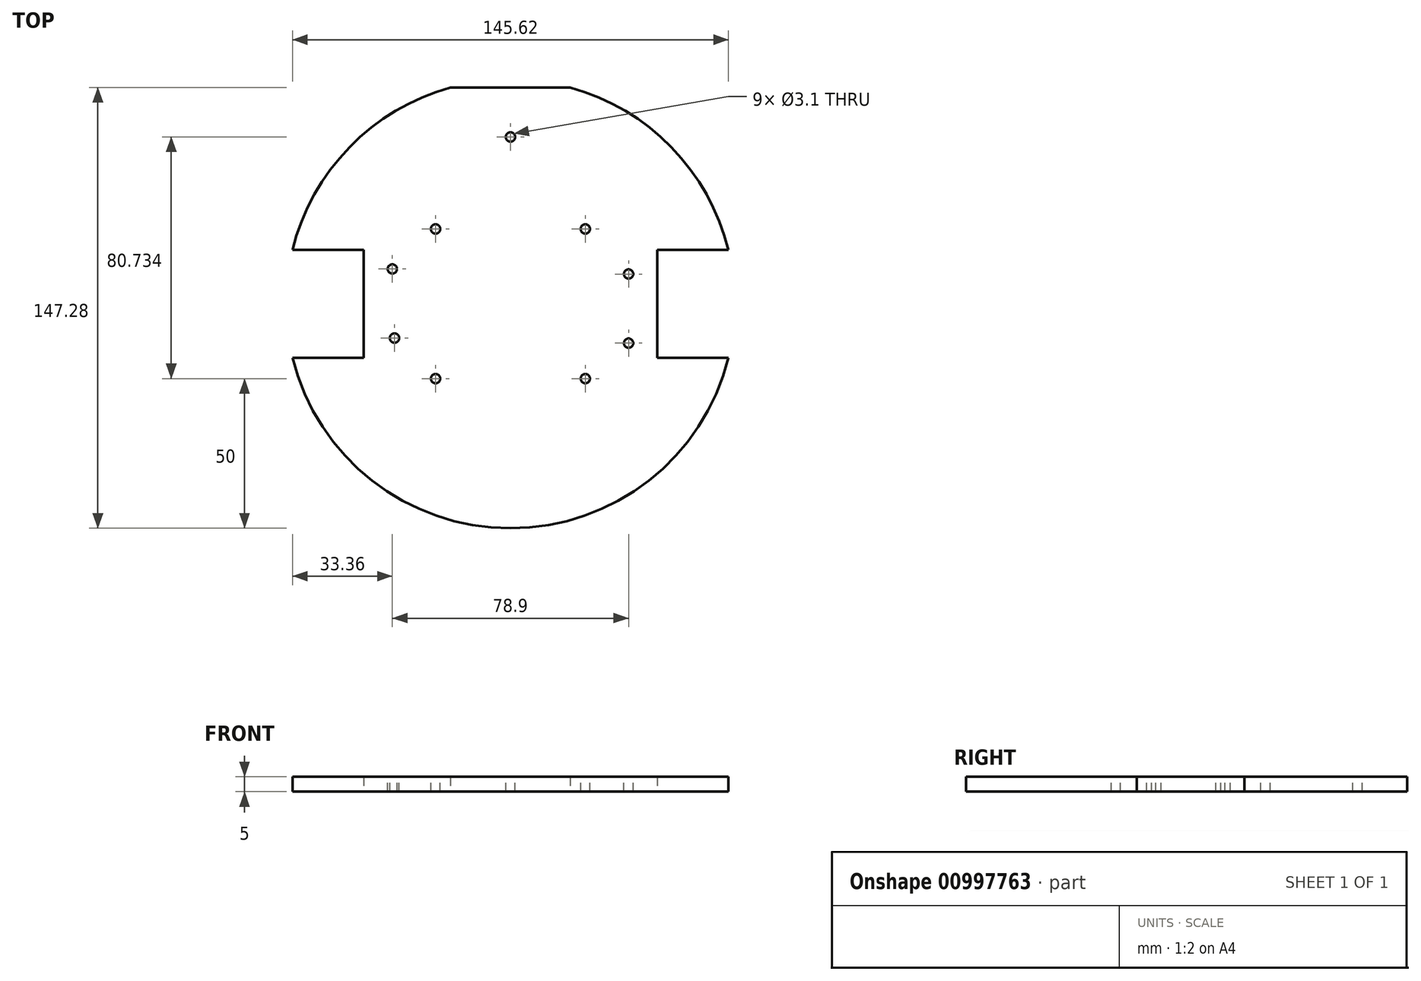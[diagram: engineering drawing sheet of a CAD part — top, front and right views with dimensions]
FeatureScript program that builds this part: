
annotation { "Feature Type Name" : "Feature", "Feature Type Description" : "" }
export const myFeature = defineFeature(function(context is Context, id is Id, definition is map)
    precondition{}
    {
        {
            var Q0;
            Q0=qCreatedBy(makeId("Top.planeOp"),FACE);
            var sketch = newSketch(context, id + "F0", { "sketchPlane" : qUnion([Q0])});
            skCircle(sketch, "E0", {"center": v(0, 0) * mm, "radius": 75 * mm});
            skSolve(sketch);
        }
        {
            var Q0;
            Q0=makeQuery(id+"F0.imprint","IMPRINT",FACE,{"disambiguationData":[TD([[makeQuery(id+"F0.imprint","IMPRINT",EDGE,{"derivedFrom":sQuery(id+"F0.wireOp",EDGE,"E0")}),1.0]])]});
            extrude(context, id + "F1", {"entities" : qUnion([Q0]), "depth" : 5 * mm, "offsetDistance" : 25 * mm});
        }
        {
            var Q0;
            Q0=qCreatedBy(makeId("Top.planeOp"),FACE);
            var sketch = newSketch(context, id + "F2", { "sketchPlane" : qUnion([Q0])});
            skLineSegment(sketch, "E1.bottom", {"start": v(75, -18) * mm, "end": v(49, -18) * mm});
            skLineSegment(sketch, "E1.top", {"start": v(75, 18) * mm, "end": v(49, 18) * mm});
            skLineSegment(sketch, "E1.left", {"start": v(75, -18) * mm, "end": v(75, 18) * mm});
            skLineSegment(sketch, "E1.right", {"start": v(49, -18) * mm, "end": v(49, 18) * mm});
            skSolve(sketch);
        }
        {
            var Q0;
            Q0=makeQuery(id+"F2.imprint","IMPRINT",FACE,{"disambiguationData":[TD([[makeQuery(id+"F2.imprint","IMPRINT",EDGE,{"derivedFrom":sQuery(id+"F2.wireOp",EDGE,"E1.bottom")}),-1.0]])]});
            extrude(context, id + "F3", {"entities" : qUnion([Q0]), "operationType" : NewBodyOperationType.REMOVE, "depth" : 25 * mm, "offsetDistance" : 25 * mm});
        }
        {
            var Q0;
            Q0=qCreatedBy(makeId("Top.planeOp"),FACE);
            var sketch = newSketch(context, id + "F4", { "sketchPlane" : qUnion([Q0])});
            skLineSegment(sketch, "E2.bottom", {"start": v(-49, -18) * mm, "end": v(-75, -18) * mm});
            skLineSegment(sketch, "E2.top", {"start": v(-49, 18) * mm, "end": v(-75, 18) * mm});
            skLineSegment(sketch, "E2.left", {"start": v(-49, -18) * mm, "end": v(-49, 18) * mm});
            skLineSegment(sketch, "E2.right", {"start": v(-75, -18) * mm, "end": v(-75, 18) * mm});
            skSolve(sketch);
        }
        {
            var Q0;
            Q0=makeQuery(id+"F4.imprint","IMPRINT",FACE,{"disambiguationData":[TD([[makeQuery(id+"F4.imprint","IMPRINT",EDGE,{"derivedFrom":sQuery(id+"F4.wireOp",EDGE,"E2.bottom")}),-1.0]])]});
            extrude(context, id + "F5", {"entities" : qUnion([Q0]), "operationType" : NewBodyOperationType.REMOVE, "depth" : 25 * mm, "offsetDistance" : 25 * mm});
        }
        {
            var Q0;
            Q0=qCreatedBy(makeId("Top.planeOp"),FACE);
            var sketch = newSketch(context, id + "F6", { "sketchPlane" : qUnion([Q0])});
            skLineSegment(sketch, "E3.bottom", {"start": v(20, 78) * mm, "end": v(-20, 78) * mm});
            skLineSegment(sketch, "E3.top", {"start": v(20, 72.28) * mm, "end": v(-20, 72.28) * mm});
            skLineSegment(sketch, "E3.left", {"start": v(20, 78) * mm, "end": v(20, 72.28) * mm});
            skLineSegment(sketch, "E3.right", {"start": v(-20, 78) * mm, "end": v(-20, 72.28) * mm});
            skSolve(sketch);
        }
        {
            var Q0;
            Q0=makeQuery(id+"F6.imprint","IMPRINT",FACE,{"disambiguationData":[TD([[makeQuery(id+"F6.imprint","IMPRINT",EDGE,{"derivedFrom":sQuery(id+"F6.wireOp",EDGE,"E3.bottom")}),1.0]])]});
            extrude(context, id + "F7", {"entities" : qUnion([Q0]), "operationType" : NewBodyOperationType.REMOVE, "depth" : 25 * mm, "offsetDistance" : 25 * mm});
        }
        {
            var Q0;
            Q0=makeQuery(id+"F1.opExtrude","CAP_FACE",FACE,{"disambiguationData":[OSD([sQuery(id+"F0.wireOp",EDGE,"E0")])],"isStart":false});
            var sketch = newSketch(context, id + "F8", { "sketchPlane" : qUnion([Q0])});
            skCircle(sketch, "E4", {"center": v(-25, 25) * mm, "radius": 1.55 * mm});
            skCircle(sketch, "E5", {"center": v(25, 25) * mm, "radius": 1.55 * mm});
            skCircle(sketch, "E6", {"center": v(-25, -25) * mm, "radius": 1.55 * mm});
            skCircle(sketch, "E7", {"center": v(25, -25) * mm, "radius": 1.55 * mm});
            skSolve(sketch);
        }
        {
            var Q0;
            Q0=makeQuery(id+"F8.imprint","IMPRINT",FACE,{"disambiguationData":[TD([[makeQuery(id+"F8.imprint","IMPRINT",EDGE,{"derivedFrom":sQuery(id+"F8.wireOp",EDGE,"E6")}),1.0]])]});
            var Q1;
            Q1=makeQuery(id+"F8.imprint","IMPRINT",FACE,{"disambiguationData":[TD([[makeQuery(id+"F8.imprint","IMPRINT",EDGE,{"derivedFrom":sQuery(id+"F8.wireOp",EDGE,"E4")}),1.0]])]});
            var Q2;
            Q2=makeQuery(id+"F8.imprint","IMPRINT",FACE,{"disambiguationData":[TD([[makeQuery(id+"F8.imprint","IMPRINT",EDGE,{"derivedFrom":sQuery(id+"F8.wireOp",EDGE,"E5")}),1.0]])]});
            var Q3;
            Q3=makeQuery(id+"F8.imprint","IMPRINT",FACE,{"disambiguationData":[TD([[makeQuery(id+"F8.imprint","IMPRINT",EDGE,{"derivedFrom":sQuery(id+"F8.wireOp",EDGE,"E7")}),1.0]])]});
            var Q4;
            Q4=sQuery(id+"F8.wireOp",EDGE,"E6");
            var Q5;
            Q5=sQuery(id+"F8.wireOp",EDGE,"E4");
            var Q6;
            Q6=sQuery(id+"F8.wireOp",EDGE,"E5");
            var Q7;
            Q7=sQuery(id+"F8.wireOp",EDGE,"E7");
            extrude(context, id + "F9", {"entities" : qUnion([Q0, Q1, Q2, Q3]), "operationType" : NewBodyOperationType.REMOVE, "surfaceEntities" : qUnion([Q4, Q5, Q6, Q7]), "oppositeDirection" : true, "depth" : 25 * mm, "offsetDistance" : 25 * mm});
        }
        {
            var Q0;
            Q0=makeQuery(id+"F1.opExtrude","CAP_FACE",FACE,{"disambiguationData":[OSD([sQuery(id+"F0.wireOp",EDGE,"E0")])],"isStart":false});
            var sketch = newSketch(context, id + "F10", { "sketchPlane" : qUnion([Q0])});
            skCircle(sketch, "E8", {"center": v(39.45, 9.95) * mm, "radius": 1.55 * mm});
            skCircle(sketch, "E9", {"center": v(39.45, -13.15) * mm, "radius": 1.55 * mm});
            skSolve(sketch);
        }
        {
            var Q0;
            Q0=makeQuery(id+"F10.imprint","IMPRINT",FACE,{"disambiguationData":[TD([[makeQuery(id+"F10.imprint","IMPRINT",EDGE,{"derivedFrom":sQuery(id+"F10.wireOp",EDGE,"E8")}),1.0]])]});
            var Q1;
            Q1=makeQuery(id+"F10.imprint","IMPRINT",FACE,{"disambiguationData":[TD([[makeQuery(id+"F10.imprint","IMPRINT",EDGE,{"derivedFrom":sQuery(id+"F10.wireOp",EDGE,"E9")}),1.0]])]});
            var Q2;
            Q2=sQuery(id+"F10.wireOp",EDGE,"E8");
            var Q3;
            Q3=sQuery(id+"F10.wireOp",EDGE,"E9");
            extrude(context, id + "F11", {"entities" : qUnion([Q0, Q1]), "operationType" : NewBodyOperationType.REMOVE, "surfaceEntities" : qUnion([Q2, Q3]), "oppositeDirection" : true, "depth" : 25 * mm, "offsetDistance" : 25 * mm});
        }
        {
            var Q0;
            Q0=makeQuery(id+"F1.opExtrude","CAP_FACE",FACE,{"disambiguationData":[OSD([sQuery(id+"F0.wireOp",EDGE,"E0")])],"isStart":false});
            var sketch = newSketch(context, id + "F12", { "sketchPlane" : qUnion([Q0])});
            skCircle(sketch, "E10", {"center": v(-39.45, 11.64) * mm, "radius": 1.55 * mm});
            skCircle(sketch, "E11", {"center": v(-38.73, -11.45) * mm, "radius": 1.55 * mm});
            skSolve(sketch);
        }
        {
            var Q0;
            Q0=makeQuery(id+"F12.imprint","IMPRINT",FACE,{"disambiguationData":[TD([[makeQuery(id+"F12.imprint","IMPRINT",EDGE,{"derivedFrom":sQuery(id+"F12.wireOp",EDGE,"E10")}),1.0]])]});
            var Q1;
            Q1=makeQuery(id+"F12.imprint","IMPRINT",FACE,{"disambiguationData":[TD([[makeQuery(id+"F12.imprint","IMPRINT",EDGE,{"derivedFrom":sQuery(id+"F12.wireOp",EDGE,"E11")}),1.0]])]});
            extrude(context, id + "F13", {"entities" : qUnion([Q0, Q1]), "operationType" : NewBodyOperationType.REMOVE, "oppositeDirection" : true, "depth" : 25 * mm, "offsetDistance" : 25 * mm});
        }
        {
            var Q0;
            Q0=makeQuery(id+"F1.opExtrude","CAP_FACE",FACE,{"disambiguationData":[OSD([sQuery(id+"F0.wireOp",EDGE,"E0")])],"isStart":false});
            var sketch = newSketch(context, id + "F14", { "sketchPlane" : qUnion([Q0])});
            skCircle(sketch, "E12", {"center": v(0, 55.73) * mm, "radius": 1.55 * mm});
            skSolve(sketch);
        }
        {
            var Q0;
            Q0=makeQuery(id+"F14.imprint","IMPRINT",FACE,{"disambiguationData":[TD([[makeQuery(id+"F14.imprint","IMPRINT",EDGE,{"derivedFrom":sQuery(id+"F14.wireOp",EDGE,"E12")}),1.0]])]});
            var Q1;
            Q1=sQuery(id+"F14.wireOp",EDGE,"E12");
            extrude(context, id + "F15", {"entities" : qUnion([Q0]), "operationType" : NewBodyOperationType.REMOVE, "surfaceEntities" : qUnion([Q1]), "oppositeDirection" : true, "depth" : 25 * mm, "offsetDistance" : 25 * mm});
        }
    });
